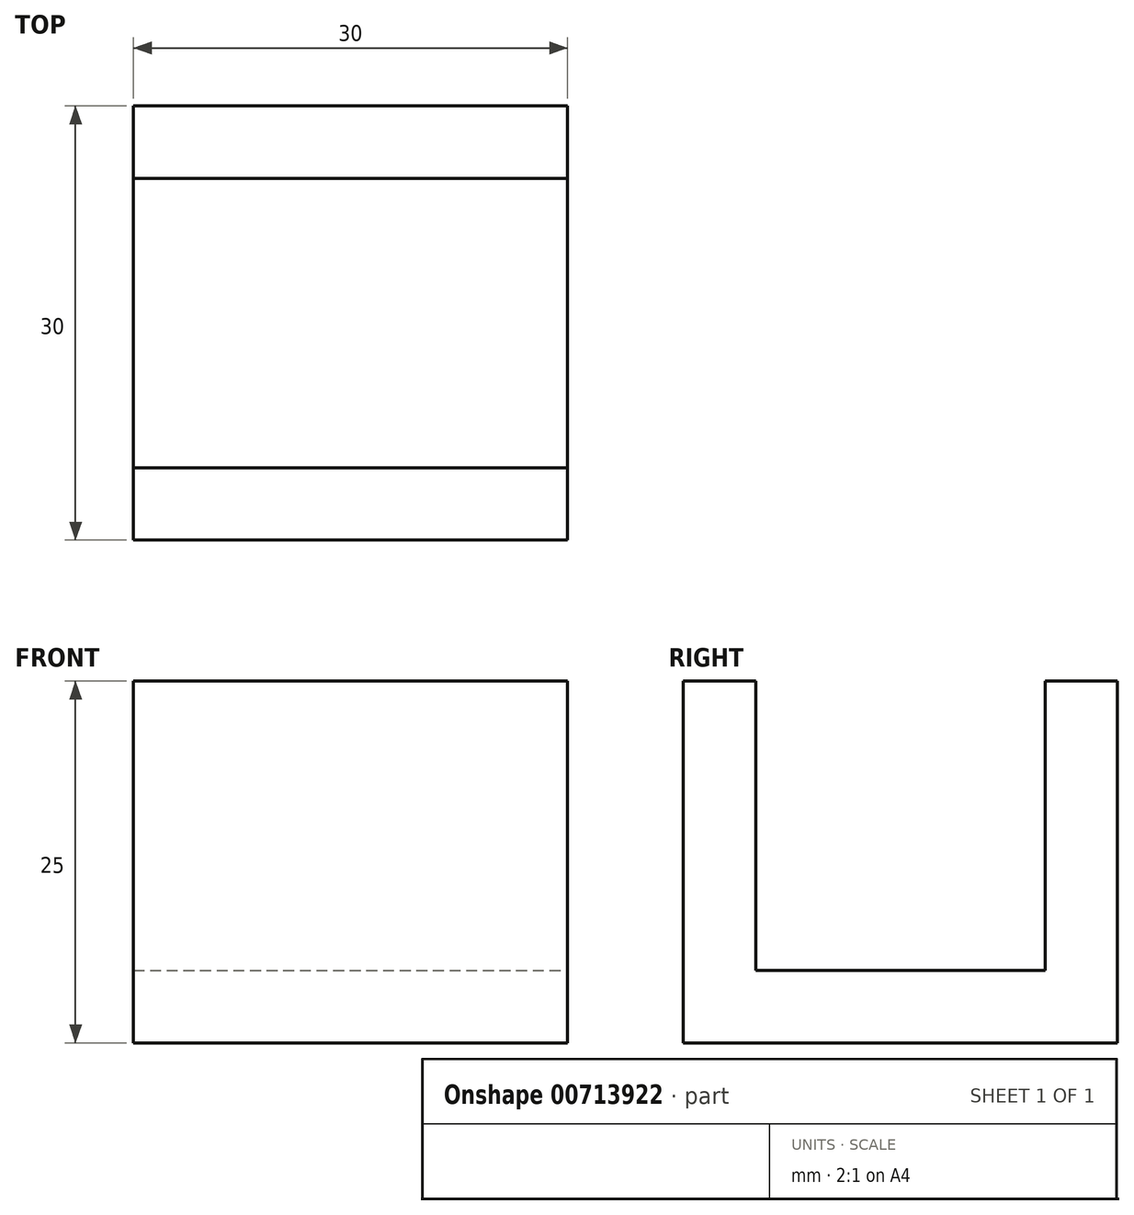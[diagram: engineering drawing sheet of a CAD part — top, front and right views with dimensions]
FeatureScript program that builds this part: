
annotation { "Feature Type Name" : "Feature", "Feature Type Description" : "" }
export const myFeature = defineFeature(function(context is Context, id is Id, definition is map)
    precondition{}
    {
        {
            var Q0;
            Q0=qCreatedBy(makeId("Top.planeOp"),FACE);
            var sketch = newSketch(context, id + "F0", { "sketchPlane" : qUnion([Q0])});
            skLineSegment(sketch, "E0.bottom", {"start": v(-21, 25) * mm, "end": v(9, 25) * mm});
            skLineSegment(sketch, "E0.top", {"start": v(-21, -5) * mm, "end": v(9, -5) * mm});
            skLineSegment(sketch, "E0.left", {"start": v(-21, 25) * mm, "end": v(-21, -5) * mm});
            skLineSegment(sketch, "E0.right", {"start": v(9, 25) * mm, "end": v(9, -5) * mm});
            skLineSegment(sketch, "E1", {"start": v(-21, 20) * mm, "end": v(9, 20) * mm});
            skLineSegment(sketch, "E2", {"start": v(9, 0) * mm, "end": v(-21, 0) * mm});
            skSolve(sketch);
        }
        {
            var Q0;
            {var subQ0=sQuery(id+"F0.wireOp",EDGE,"E1");Q0=makeQuery(id+"F0.imprint","IMPRINT",FACE,{"disambiguationData":[TD([[makeQuery(id+"F0.imprint","IMPRINT",EDGE,{"derivedFrom":subQ0}),-1.0]])]});}
            extrude(context, id + "F1", {"entities" : qUnion([Q0]), "depth" : 5 * mm, "offsetDistance" : 25 * mm});
        }
        {
            var Q0;
            {var subQ0=sQuery(id+"F0.wireOp",EDGE,"E0.bottom");Q0=makeQuery(id+"F0.imprint","IMPRINT",FACE,{"disambiguationData":[TD([[makeQuery(id+"F0.imprint","IMPRINT",EDGE,{"derivedFrom":subQ0}),-1.0]])]});}
            var Q1;
            {var subQ0=sQuery(id+"F0.wireOp",EDGE,"E0.top");Q1=makeQuery(id+"F0.imprint","IMPRINT",FACE,{"disambiguationData":[TD([[makeQuery(id+"F0.imprint","IMPRINT",EDGE,{"derivedFrom":subQ0}),1.0]])]});}
            extrude(context, id + "F2", {"entities" : qUnion([Q0, Q1]), "operationType" : NewBodyOperationType.ADD, "depth" : 25 * mm, "offsetDistance" : 25 * mm});
        }
    });
